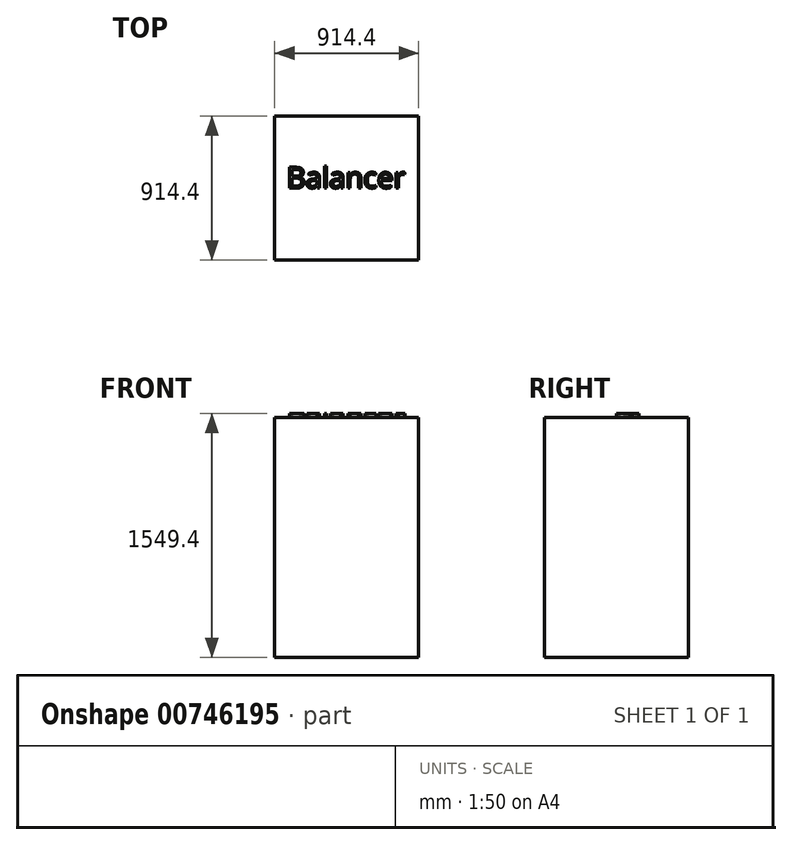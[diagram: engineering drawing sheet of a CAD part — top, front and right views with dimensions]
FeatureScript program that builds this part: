
annotation { "Feature Type Name" : "Feature", "Feature Type Description" : "" }
export const myFeature = defineFeature(function(context is Context, id is Id, definition is map)
    precondition{}
    {
        {
            var Q0;
            Q0=qCreatedBy(makeId("Top.planeOp"),FACE);
            var sketch = newSketch(context, id + "F0", { "sketchPlane" : qUnion([Q0])});
            skLineSegment(sketch, "E0.bottom", {"start": v(457.2, -457.2) * mm, "end": v(-457.2, -457.2) * mm});
            skLineSegment(sketch, "E0.top", {"start": v(457.2, 457.2) * mm, "end": v(-457.2, 457.2) * mm});
            skLineSegment(sketch, "E0.left", {"start": v(457.2, -457.2) * mm, "end": v(457.2, 457.2) * mm});
            skLineSegment(sketch, "E0.right", {"start": v(-457.2, -457.2) * mm, "end": v(-457.2, 457.2) * mm});
            skPoint(sketch, "E0.middle", {"position": v(0, 0) * mm});
            skSolve(sketch);
        }
        {
            var Q0;
            Q0 = qSketchRegion(id + "F0", true);
            extrude(context, id + "F1", {"entities" : qUnion([Q0]), "depth" : 1524 * mm, "offsetDistance" : 25.4 * mm});
        }
        {
            var Q0;
            Q0=makeQuery(id+"F1.opExtrude","CAP_FACE",FACE,{"disambiguationData":[OSD([sQuery(id+"F0.wireOp",EDGE,"E0.bottom"),sQuery(id+"F0.wireOp",EDGE,"E0.top"),sQuery(id+"F0.wireOp",EDGE,"E0.left"),sQuery(id+"F0.wireOp",EDGE,"E0.right")])],"isStart":false});
            var sketch = newSketch(context, id + "F2", { "sketchPlane" : qUnion([Q0])});
            skText(sketch, "E1", { "text": "Balancer", "fontName": "OpenSans-Regular.ttf"});
            const initialGuessF2  = {"E1": [-0.381, 0, 1, 0, 0.13307]};
            skSetInitialGuess(sketch, initialGuessF2);
            skSolve(sketch);
        }
        {
            var Q0;
            Q0 = qSketchRegion(id + "F2", true);
            extrude(context, id + "F3", {"entities" : qUnion([Q0]), "operationType" : NewBodyOperationType.ADD, "depth" : 25.4 * mm, "offsetDistance" : 25.4 * mm});
        }
    });
